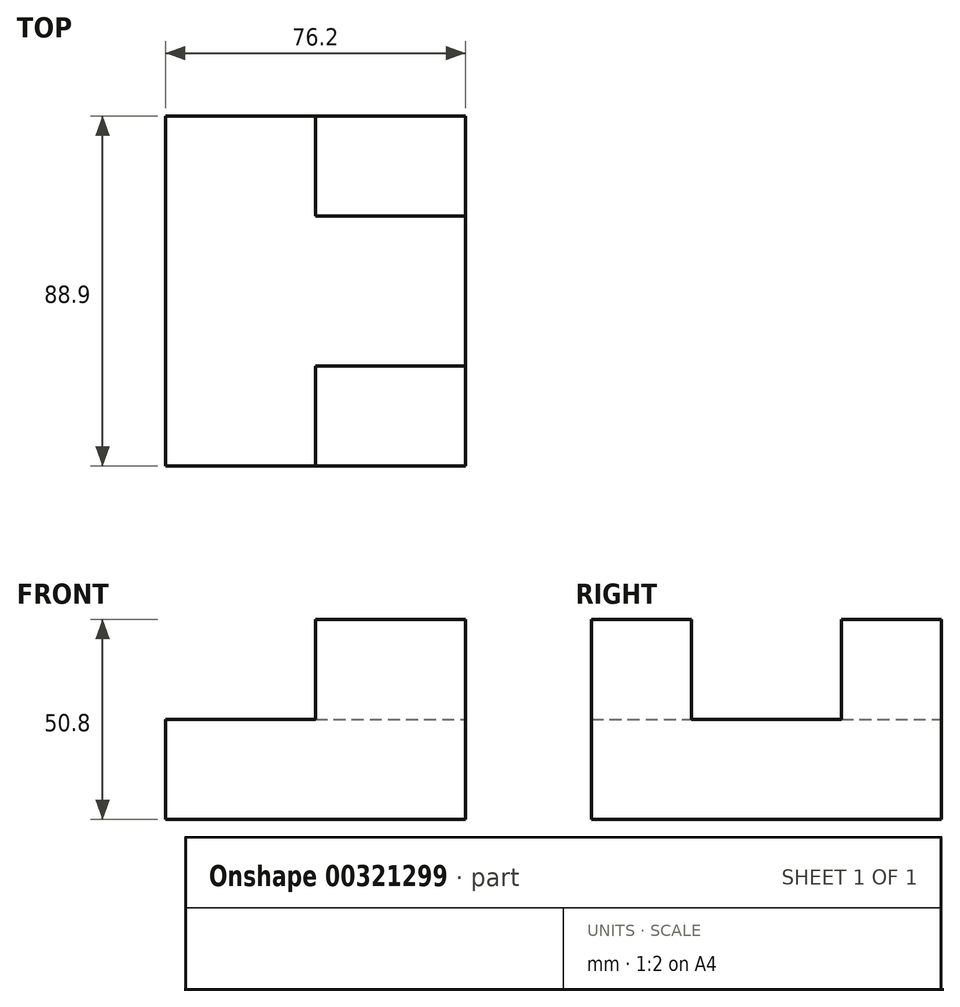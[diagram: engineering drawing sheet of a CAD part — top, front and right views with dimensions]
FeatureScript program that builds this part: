
annotation { "Feature Type Name" : "Feature", "Feature Type Description" : "" }
export const myFeature = defineFeature(function(context is Context, id is Id, definition is map)
    precondition{}
    {
        {
            var Q0;
            Q0=qCreatedBy(makeId("Front.planeOp"),FACE);
            var sketch = newSketch(context, id + "F0", { "sketchPlane" : qUnion([Q0])});
            skLineSegment(sketch, "E0", {"start": v(-48.68, -42.15) * mm, "end": v(27.52, -42.15) * mm});
            skLineSegment(sketch, "E1", {"start": v(27.52, -42.15) * mm, "end": v(27.52, 8.65) * mm});
            skLineSegment(sketch, "E2", {"start": v(27.52, 8.65) * mm, "end": v(-10.58, 8.65) * mm});
            skLineSegment(sketch, "E3", {"start": v(-10.58, 8.65) * mm, "end": v(-10.58, -16.75) * mm});
            skLineSegment(sketch, "E4", {"start": v(-48.68, -42.15) * mm, "end": v(-48.68, -16.75) * mm});
            skLineSegment(sketch, "E5", {"start": v(-48.68, -16.75) * mm, "end": v(-10.58, -16.75) * mm});
            skSolve(sketch);
        }
        {
            var Q0;
            Q0 = qSketchRegion(id + "F0", true);
            extrude(context, id + "F1", {"entities" : qUnion([Q0]), "depth" : 88.9 * mm});
        }
        {
            var Q0;
            Q0=makeQuery(id+"F1.opExtrude","SWEPT_FACE",FACE,{"disambiguationData":[OSD([sQuery(id+"F0.wireOp",EDGE,"E2")])]});
            var sketch = newSketch(context, id + "F2", { "sketchPlane" : qUnion([Q0])});
            skLineSegment(sketch, "E6", {"start": v(27.52, -25.4) * mm, "end": v(-10.58, -25.4) * mm});
            skLineSegment(sketch, "E7", {"start": v(-10.58, -25.4) * mm, "end": v(-10.58, -63.5) * mm});
            skLineSegment(sketch, "E8", {"start": v(-10.58, -63.5) * mm, "end": v(27.52, -63.5) * mm});
            skLineSegment(sketch, "E9", {"start": v(27.52, -25.4) * mm, "end": v(27.52, -63.5) * mm});
            skSolve(sketch);
        }
        {
            var Q0;
            Q0 = qSketchRegion(id + "F2", true);
            extrude(context, id + "F3", {"entities" : qUnion([Q0]), "operationType" : NewBodyOperationType.REMOVE, "oppositeDirection" : true, "depth" : 25.4 * mm});
        }
    });
